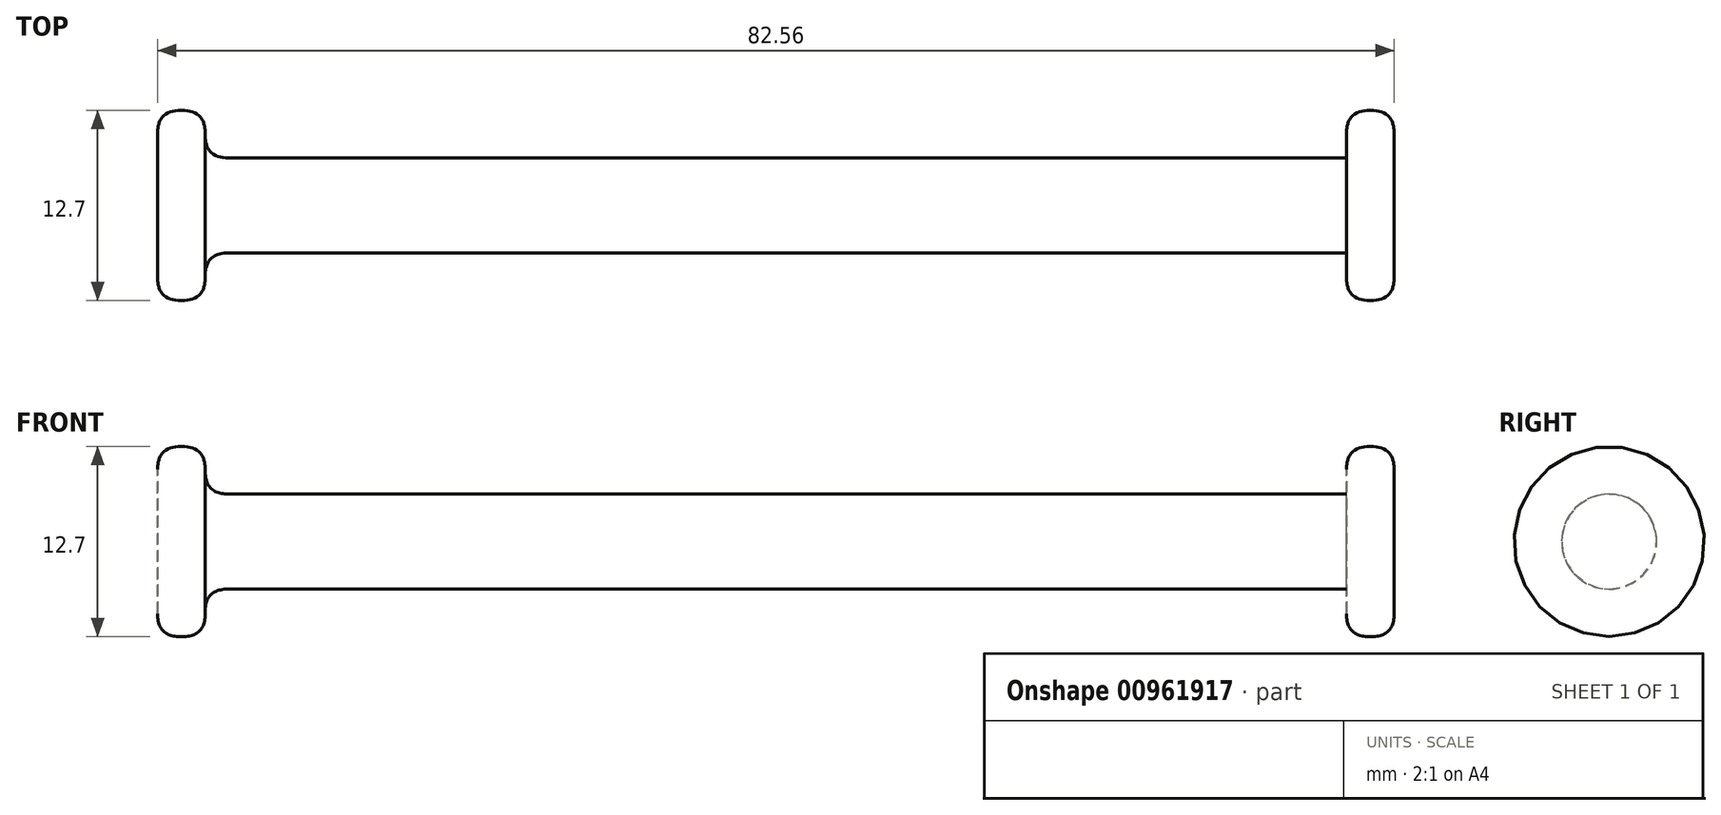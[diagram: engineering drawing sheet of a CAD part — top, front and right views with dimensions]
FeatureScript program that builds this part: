
annotation { "Feature Type Name" : "Feature", "Feature Type Description" : "" }
export const myFeature = defineFeature(function(context is Context, id is Id, definition is map)
    precondition{}
    {
        {
            var Q0;
            Q0=qCreatedBy(makeId("Right.planeOp"),FACE);
            var sketch = newSketch(context, id + "F0", { "sketchPlane" : qUnion([Q0])});
            skCircle(sketch, "E0", {"center": v(0, 0) * mm, "radius": 3.18 * mm});
            skSolve(sketch);
        }
        {
            var Q0;
            Q0 = qSketchRegion(id + "F0", true);
            extrude(context, id + "F1", {"entities" : qUnion([Q0]), "endBound" : BoundingType.SYMMETRIC, "depth" : 76.2 * mm, "offsetDistance" : 25.4 * mm});
        }
        {
            var Q0;
            Q0=makeQuery(id+"F1.opExtrude","CAP_FACE",FACE,{"disambiguationData":[OSD([sQuery(id+"F0.wireOp",EDGE,"E0")])],"isStart":false});
            var sketch = newSketch(context, id + "F2", { "sketchPlane" : qUnion([Q0])});
            skCircle(sketch, "E1", {"center": v(0, 0) * mm, "radius": 6.35 * mm});
            skSolve(sketch);
        }
        {
            var Q0;
            Q0 = qSketchRegion(id + "F2", true);
            extrude(context, id + "F3", {"entities" : qUnion([Q0]), "operationType" : NewBodyOperationType.ADD, "depth" : 3.17 * mm, "offsetDistance" : 25.4 * mm});
        }
        {
            var Q0;
            Q0=makeQuery(id+"F1.opExtrude","SWEPT_BODY",BODY,{"disambiguationData":[OSD([sQuery(id+"F0.wireOp",EDGE,"E0")])]});
            var Q1;
            Q1=qCreatedBy(makeId("Right.planeOp"),FACE);
            mirror(context, id + "F4", {"operationType" : NewBodyOperationType.ADD, "entities" : qUnion([Q0]), "mirrorPlane" : qUnion([Q1])});
        }
        {
            var Q0;
            {var subQ0=sQuery(id+"F0.wireOp",EDGE,"E0");Q0=makeQuery(id+"F4.boolean.opBoolean","MERGE",EDGE,{"derivedFrom":[makeQuery(id+"F1.opExtrude","CAP_EDGE",EDGE,{"disambiguationData":[OSD([subQ0])],"isStart":true}),makeQuery(id+"F4.opPattern","COPY",EDGE,{"derivedFrom":makeQuery(id+"F1.opExtrude","CAP_EDGE",EDGE,{"disambiguationData":[OSD([subQ0])],"isStart":false}),"instanceName":"1"})]});}
            var Q1;
            Q1=makeQuery(id+"F1.opExtrude","CAP_EDGE",EDGE,{"disambiguationData":[OSD([sQuery(id+"F0.wireOp",EDGE,"E0")])],"isStart":false});
            var Q2;
            Q2=makeQuery(id+"F3.opExtrude","CAP_EDGE",EDGE,{"disambiguationData":[OSD([sQuery(id+"F2.wireOp",EDGE,"E1")])],"isStart":true});
            var Q3;
            Q3=makeQuery(id+"F3.opExtrude","CAP_EDGE",EDGE,{"disambiguationData":[OSD([sQuery(id+"F2.wireOp",EDGE,"E1")])],"isStart":false});
            var Q4;
            Q4=makeQuery(id+"F4.opPattern","COPY",FACE,{"derivedFrom":makeQuery(id+"F3.opExtrude","SWEPT_FACE",FACE,{"disambiguationData":[OSD([sQuery(id+"F2.wireOp",EDGE,"E1")])]}),"instanceName":"1"});
            fillet(context, id + "F5", {"entities" : qUnion([Q0, Q1, Q2, Q3, Q4]), "radius" : 1.52 * mm, "tangentPropagation" : true, "rho" : 0.5, "crossSection" : FilletCrossSection.CONIC, "allowEdgeOverflow" : false});
        }
    });
